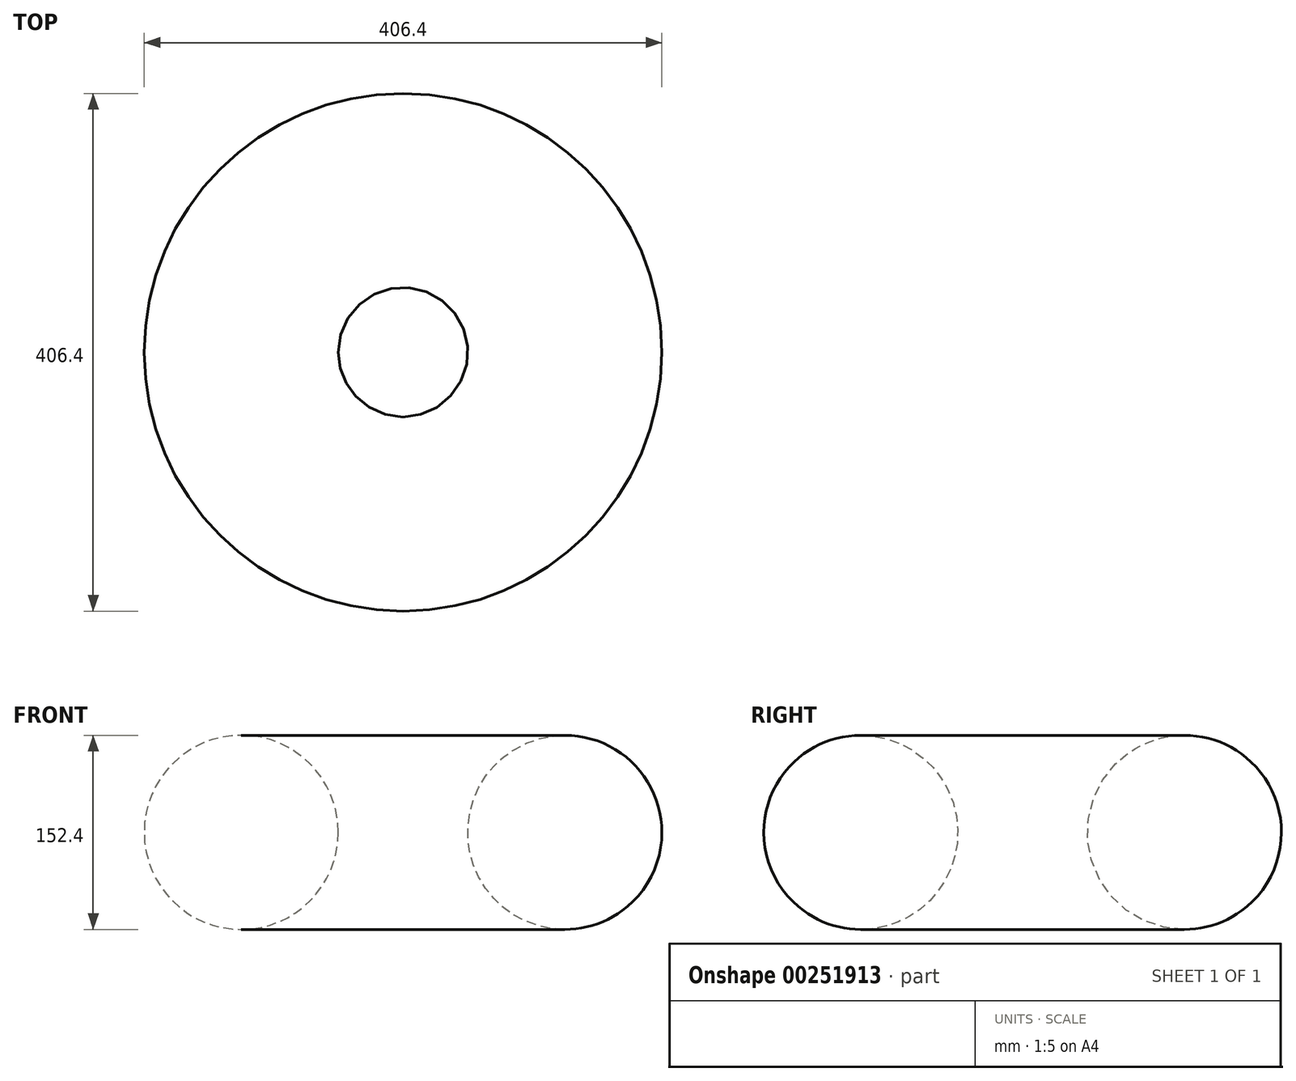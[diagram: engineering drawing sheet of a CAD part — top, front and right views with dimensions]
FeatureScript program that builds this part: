
annotation { "Feature Type Name" : "Feature", "Feature Type Description" : "" }
export const myFeature = defineFeature(function(context is Context, id is Id, definition is map)
    precondition{}
    {
        {
            var Q0;
            Q0=qCreatedBy(makeId("Front.planeOp"),FACE);
            var sketch = newSketch(context, id + "F0", { "sketchPlane" : qUnion([Q0])});
            skCircle(sketch, "E0", {"center": v(-127, 16.67) * mm, "radius": 76.2 * mm});
            skSolve(sketch);
        }
        {
            var Q0;
            Q0=qCreatedBy(makeId("Front.planeOp"),FACE);
            var sketch = newSketch(context, id + "F1", { "sketchPlane" : qUnion([Q0])});
            skLineSegment(sketch, "E1", {"start": v(0, 0) * mm, "end": v(0, 92.18) * mm, "construction": true});
            skSolve(sketch);
        }
        {
            var Q0;
            Q0=makeQuery(id+"F0.imprint","IMPRINT",FACE,{"disambiguationData":[TD([[makeQuery(id+"F0.imprint","IMPRINT",EDGE,{"derivedFrom":sQuery(id+"F0.wireOp",EDGE,"E0")}),1.0]])]});
            var Q1;
            Q1=sQuery(id+"F1.wireOp",EDGE,"E1");
            revolve(context, id + "F2", {"entities" : qUnion([Q0]), "axis" : qUnion([Q1]), "revolveType" : RevolveType.FULL});
        }
    });
